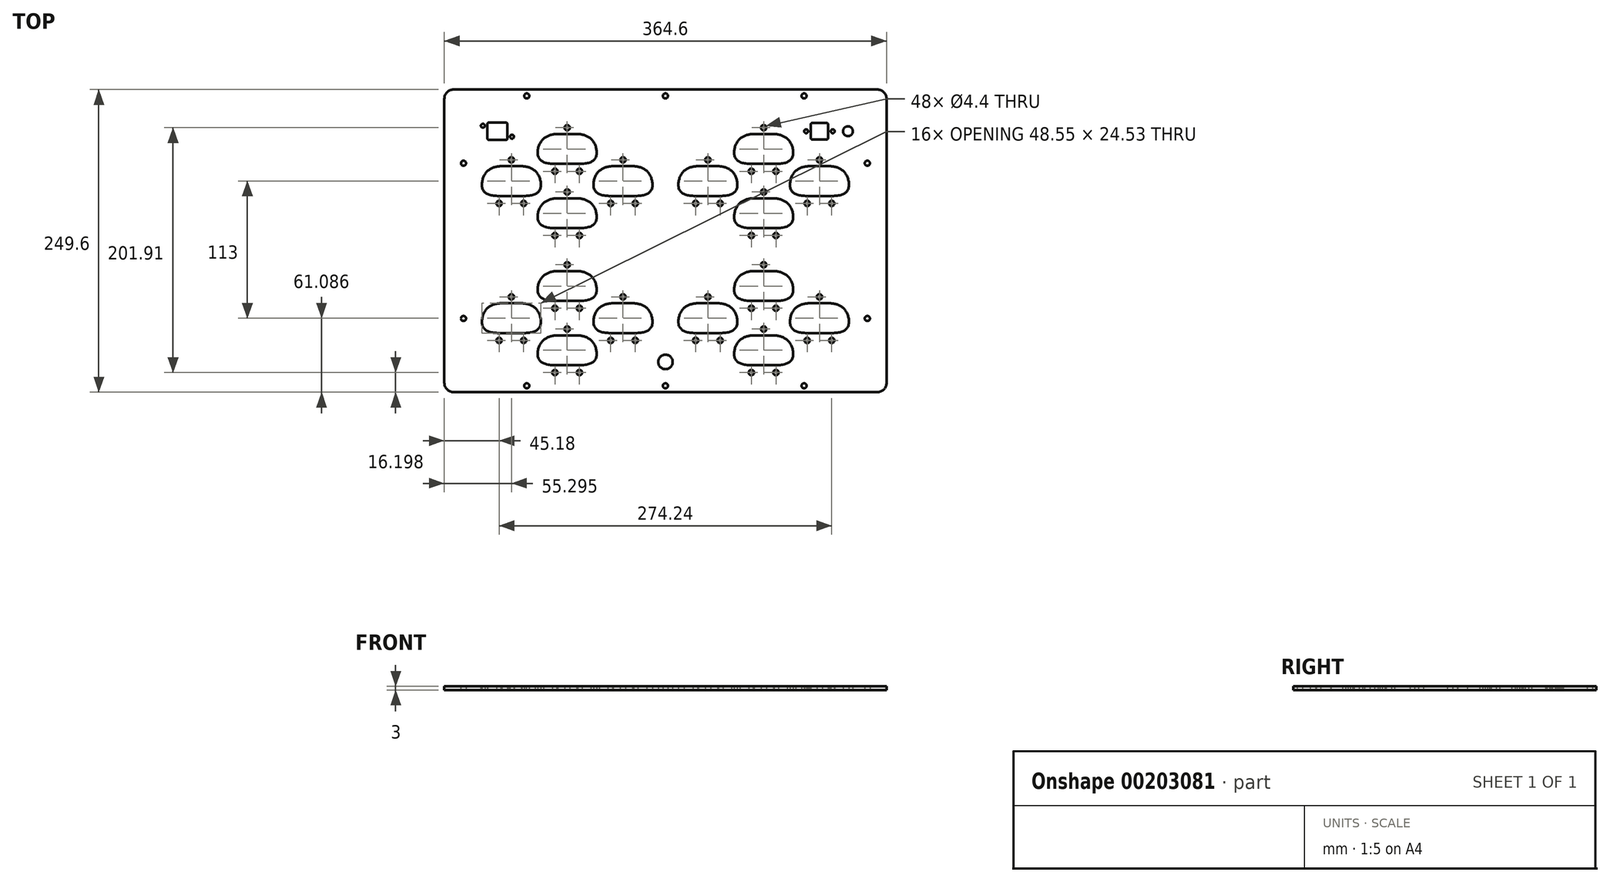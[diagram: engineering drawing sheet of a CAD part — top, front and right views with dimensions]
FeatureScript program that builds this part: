
annotation { "Feature Type Name" : "Feature", "Feature Type Description" : "" }
export const myFeature = defineFeature(function(context is Context, id is Id, definition is map)
    precondition{}
    {
        {
            var Q0;
            Q0=qCreatedBy(makeId("Top.planeOp"),FACE);
            var sketch = newSketch(context, id + "F0", { "sketchPlane" : qUnion([Q0])});
            skLineSegment(sketch, "E0.bottom", {"start": v(-174.5, 124.8) * mm, "end": v(174.5, 124.8) * mm});
            skLineSegment(sketch, "E0.top", {"start": v(-174.5, -124.8) * mm, "end": v(174.5, -124.8) * mm});
            skLineSegment(sketch, "E0.left", {"start": v(-182.3, 117) * mm, "end": v(-182.3, -117) * mm});
            skLineSegment(sketch, "E0.right", {"start": v(182.3, 117) * mm, "end": v(182.3, -117) * mm});
            skPoint(sketch, "E1.visualSharp", {"position": v(-182.3, 124.8) * mm});
            skArc(sketch, "E1.filletArc", {"start": v(-174.5, 124.8) * mm, "mid": v(-180.02, 122.52) * mm, "end": v(-182.3, 117) * mm});
            skPoint(sketch, "E2.visualSharp", {"position": v(182.3, 124.8) * mm});
            skArc(sketch, "E2.filletArc", {"start": v(182.3, 117) * mm, "mid": v(180.02, 122.52) * mm, "end": v(174.5, 124.8) * mm});
            skPoint(sketch, "E3.visualSharp", {"position": v(182.3, -124.8) * mm});
            skArc(sketch, "E3.filletArc", {"start": v(174.5, -124.8) * mm, "mid": v(180.02, -122.52) * mm, "end": v(182.3, -117) * mm});
            skPoint(sketch, "E4.visualSharp", {"position": v(-182.3, -124.8) * mm});
            skArc(sketch, "E4.filletArc", {"start": v(-182.3, -117) * mm, "mid": v(-180.02, -122.52) * mm, "end": v(-174.5, -124.8) * mm});
            skCircle(sketch, "E5", {"center": v(-166.5, -64) * mm, "radius": 2.1 * mm});
            skCircle(sketch, "E6", {"center": v(-166.5, 64) * mm, "radius": 2.1 * mm});
            skCircle(sketch, "E7.MirrorC", {"center": v(166.5, 64) * mm, "radius": 2.1 * mm});
            skCircle(sketch, "E8.MirrorC", {"center": v(166.5, -64) * mm, "radius": 2.1 * mm});
            skCircle(sketch, "E9", {"center": v(-114.33, -119.5) * mm, "radius": 2.1 * mm});
            skCircle(sketch, "E10", {"center": v(0, -119.5) * mm, "radius": 2.1 * mm});
            skCircle(sketch, "E11.MirrorC", {"center": v(114.33, -119.5) * mm, "radius": 2.1 * mm});
            skCircle(sketch, "E12.MirrorC", {"center": v(-114.33, 119.5) * mm, "radius": 2.1 * mm});
            skCircle(sketch, "E13.MirrorC", {"center": v(0, 119.5) * mm, "radius": 2.1 * mm});
            skCircle(sketch, "E14.MirrorC", {"center": v(114.33, 119.5) * mm, "radius": 2.1 * mm});
            skLineSegment(sketch, "E15.1", {"start": v(-135.12, -51.46) * mm, "end": v(-118.9, -51.46) * mm});
            skLineSegment(sketch, "E15.3", {"start": v(-118.9, -51.46) * mm, "end": v(-118.33, -51.45) * mm});
            skArc(sketch, "E15.4", {"start": v(-118.33, -51.45) * mm, "mid": v(-112.6, -52.41) * mm, "end": v(-107.49, -55.2) * mm});
            skArc(sketch, "E15.5", {"start": v(-107.49, -55.2) * mm, "mid": v(-103.73, -60.96) * mm, "end": v(-102.78, -67.78) * mm});
            skLineSegment(sketch, "E15.8", {"start": v(-135.1, -75.97) * mm, "end": v(-118.9, -75.97) * mm});
            skFitSpline(sketch, "E15.9", {"points": [v(-102.78, -67.78) * mm, v(-102.83, -68.48) * mm, v(-103.13, -69.85) * mm, v(-104.12, -71.74) * mm, v(-105.36, -73.07) * mm, v(-106.59, -73.94) * mm, v(-107.95, -74.65) * mm, v(-109.89, -75.3) * mm, v(-112.56, -75.75) * mm, v(-115.56, -75.96) * mm, v(-117.76, -75.98) * mm, v(-118.9, -75.97) * mm]});
            skCircle(sketch, "E16", {"center": v(-127, -46.2) * mm, "radius": 2.2 * mm});
            skCircle(sketch, "E17", {"center": v(-137.12, -82.1) * mm, "radius": 2.2 * mm});
            skCircle(sketch, "E18", {"center": v(-116.88, -82.1) * mm, "radius": 2.2 * mm});
            skFitSpline(sketch, "E19.0", {"points": [v(-151.23, -67.78) * mm, v(-151.18, -68.48) * mm, v(-150.87, -69.85) * mm, v(-149.88, -71.74) * mm, v(-148.63, -73.07) * mm, v(-147.4, -73.93) * mm, v(-146.05, -74.65) * mm, v(-144.11, -75.3) * mm, v(-141.44, -75.75) * mm, v(-138.45, -75.95) * mm, v(-136.25, -75.98) * mm, v(-135.1, -75.97) * mm]});
            skArc(sketch, "E19.1", {"start": v(-146.52, -55.2) * mm, "mid": v(-150.28, -60.96) * mm, "end": v(-151.23, -67.78) * mm});
            skArc(sketch, "E19.2", {"start": v(-135.66, -51.45) * mm, "mid": v(-141.4, -52.41) * mm, "end": v(-146.52, -55.2) * mm});
            skLineSegment(sketch, "E20.0", {"start": v(-135.1, -51.46) * mm, "end": v(-135.66, -51.45) * mm});
            skPoint(sketch, "E21", {"position": v(-156, -112.5) * mm});
            skLineSegment(sketch, "E22.1", {"start": v(-89.12, -77.96) * mm, "end": v(-72.9, -77.96) * mm});
            skLineSegment(sketch, "E22.3", {"start": v(-72.9, -77.96) * mm, "end": v(-72.33, -77.95) * mm});
            skArc(sketch, "E22.4", {"start": v(-72.33, -77.95) * mm, "mid": v(-66.6, -78.91) * mm, "end": v(-61.49, -81.7) * mm});
            skArc(sketch, "E22.5", {"start": v(-61.49, -81.7) * mm, "mid": v(-57.73, -87.46) * mm, "end": v(-56.78, -94.28) * mm});
            skLineSegment(sketch, "E22.8", {"start": v(-89.1, -102.47) * mm, "end": v(-72.9, -102.47) * mm});
            skFitSpline(sketch, "E22.9", {"points": [v(-56.78, -94.28) * mm, v(-56.83, -94.98) * mm, v(-57.13, -96.35) * mm, v(-58.12, -98.24) * mm, v(-59.36, -99.57) * mm, v(-60.58, -100.44) * mm, v(-61.95, -101.15) * mm, v(-63.88, -101.8) * mm, v(-66.56, -102.25) * mm, v(-69.56, -102.45) * mm, v(-71.76, -102.48) * mm, v(-72.9, -102.47) * mm]});
            skCircle(sketch, "E23", {"center": v(-81, -72.7) * mm, "radius": 2.2 * mm});
            skCircle(sketch, "E24", {"center": v(-91.12, -108.6) * mm, "radius": 2.2 * mm});
            skCircle(sketch, "E25", {"center": v(-70.88, -108.6) * mm, "radius": 2.2 * mm});
            skFitSpline(sketch, "E26.0", {"points": [v(-105.23, -94.28) * mm, v(-105.18, -94.98) * mm, v(-104.87, -96.35) * mm, v(-103.88, -98.24) * mm, v(-102.63, -99.57) * mm, v(-101.4, -100.43) * mm, v(-100.05, -101.15) * mm, v(-98.11, -101.8) * mm, v(-95.44, -102.25) * mm, v(-92.45, -102.45) * mm, v(-90.25, -102.48) * mm, v(-89.1, -102.47) * mm]});
            skArc(sketch, "E26.1", {"start": v(-100.52, -81.7) * mm, "mid": v(-104.28, -87.46) * mm, "end": v(-105.23, -94.28) * mm});
            skArc(sketch, "E26.2", {"start": v(-89.66, -77.95) * mm, "mid": v(-95.4, -78.91) * mm, "end": v(-100.52, -81.7) * mm});
            skLineSegment(sketch, "E27.0", {"start": v(-89.1, -77.96) * mm, "end": v(-89.66, -77.95) * mm});
            skLineSegment(sketch, "E28.1", {"start": v(-43.12, -51.46) * mm, "end": v(-26.9, -51.46) * mm});
            skLineSegment(sketch, "E28.3", {"start": v(-26.9, -51.46) * mm, "end": v(-26.33, -51.45) * mm});
            skArc(sketch, "E28.4", {"start": v(-26.33, -51.45) * mm, "mid": v(-20.6, -52.41) * mm, "end": v(-15.49, -55.2) * mm});
            skArc(sketch, "E28.5", {"start": v(-15.49, -55.2) * mm, "mid": v(-11.73, -60.96) * mm, "end": v(-10.78, -67.78) * mm});
            skLineSegment(sketch, "E28.8", {"start": v(-43.1, -75.97) * mm, "end": v(-26.9, -75.97) * mm});
            skFitSpline(sketch, "E28.9", {"points": [v(-10.78, -67.78) * mm, v(-10.83, -68.48) * mm, v(-11.13, -69.85) * mm, v(-12.12, -71.74) * mm, v(-13.36, -73.07) * mm, v(-14.59, -73.94) * mm, v(-15.95, -74.65) * mm, v(-17.89, -75.3) * mm, v(-20.56, -75.75) * mm, v(-23.56, -75.96) * mm, v(-25.76, -75.98) * mm, v(-26.9, -75.97) * mm]});
            skCircle(sketch, "E29", {"center": v(-35, -46.2) * mm, "radius": 2.2 * mm});
            skCircle(sketch, "E30", {"center": v(-45.12, -82.1) * mm, "radius": 2.2 * mm});
            skCircle(sketch, "E31", {"center": v(-24.88, -82.1) * mm, "radius": 2.2 * mm});
            skFitSpline(sketch, "E32.0", {"points": [v(-59.23, -67.78) * mm, v(-59.18, -68.48) * mm, v(-58.87, -69.85) * mm, v(-57.88, -71.74) * mm, v(-56.63, -73.07) * mm, v(-55.4, -73.93) * mm, v(-54.05, -74.65) * mm, v(-52.11, -75.3) * mm, v(-49.44, -75.75) * mm, v(-46.45, -75.95) * mm, v(-44.25, -75.98) * mm, v(-43.1, -75.97) * mm]});
            skArc(sketch, "E32.1", {"start": v(-54.52, -55.2) * mm, "mid": v(-58.28, -60.96) * mm, "end": v(-59.23, -67.78) * mm});
            skArc(sketch, "E32.2", {"start": v(-43.66, -51.45) * mm, "mid": v(-49.4, -52.41) * mm, "end": v(-54.52, -55.2) * mm});
            skLineSegment(sketch, "E33.0", {"start": v(-43.1, -51.46) * mm, "end": v(-43.66, -51.45) * mm});
            skLineSegment(sketch, "E34.1", {"start": v(-89.12, -24.96) * mm, "end": v(-72.9, -24.96) * mm});
            skLineSegment(sketch, "E34.3", {"start": v(-72.9, -24.96) * mm, "end": v(-72.33, -24.95) * mm});
            skArc(sketch, "E34.4", {"start": v(-72.33, -24.95) * mm, "mid": v(-66.6, -25.91) * mm, "end": v(-61.49, -28.7) * mm});
            skArc(sketch, "E34.5", {"start": v(-61.49, -28.7) * mm, "mid": v(-57.73, -34.46) * mm, "end": v(-56.78, -41.28) * mm});
            skLineSegment(sketch, "E34.8", {"start": v(-89.1, -49.47) * mm, "end": v(-72.9, -49.47) * mm});
            skFitSpline(sketch, "E34.9", {"points": [v(-56.78, -41.28) * mm, v(-56.83, -41.98) * mm, v(-57.13, -43.35) * mm, v(-58.12, -45.24) * mm, v(-59.36, -46.57) * mm, v(-60.59, -47.44) * mm, v(-61.95, -48.15) * mm, v(-63.89, -48.8) * mm, v(-66.56, -49.25) * mm, v(-69.56, -49.46) * mm, v(-71.76, -49.48) * mm, v(-72.9, -49.47) * mm]});
            skCircle(sketch, "E35", {"center": v(-81, -19.7) * mm, "radius": 2.2 * mm});
            skCircle(sketch, "E36", {"center": v(-91.12, -55.6) * mm, "radius": 2.2 * mm});
            skCircle(sketch, "E37", {"center": v(-70.88, -55.6) * mm, "radius": 2.2 * mm});
            skFitSpline(sketch, "E38.0", {"points": [v(-105.23, -41.28) * mm, v(-105.18, -41.98) * mm, v(-104.87, -43.35) * mm, v(-103.88, -45.24) * mm, v(-102.63, -46.57) * mm, v(-101.4, -47.43) * mm, v(-100.05, -48.15) * mm, v(-98.11, -48.8) * mm, v(-95.44, -49.25) * mm, v(-92.45, -49.45) * mm, v(-90.25, -49.48) * mm, v(-89.1, -49.47) * mm]});
            skArc(sketch, "E38.1", {"start": v(-100.52, -28.7) * mm, "mid": v(-104.28, -34.46) * mm, "end": v(-105.23, -41.28) * mm});
            skArc(sketch, "E38.2", {"start": v(-89.66, -24.95) * mm, "mid": v(-95.4, -25.91) * mm, "end": v(-100.52, -28.7) * mm});
            skLineSegment(sketch, "E39.0", {"start": v(-89.1, -24.96) * mm, "end": v(-89.66, -24.95) * mm});
            skLineSegment(sketch, "E40.1", {"start": v(-135.12, 61.54) * mm, "end": v(-118.9, 61.54) * mm});
            skLineSegment(sketch, "E40.3", {"start": v(-118.9, 61.54) * mm, "end": v(-118.33, 61.55) * mm});
            skArc(sketch, "E40.4", {"start": v(-118.33, 61.55) * mm, "mid": v(-112.6, 60.59) * mm, "end": v(-107.49, 57.8) * mm});
            skArc(sketch, "E40.5", {"start": v(-107.49, 57.8) * mm, "mid": v(-103.73, 52.04) * mm, "end": v(-102.78, 45.22) * mm});
            skLineSegment(sketch, "E40.8", {"start": v(-135.1, 37.03) * mm, "end": v(-118.9, 37.03) * mm});
            skFitSpline(sketch, "E40.9", {"points": [v(-102.78, 45.22) * mm, v(-102.83, 44.52) * mm, v(-103.13, 43.15) * mm, v(-104.12, 41.26) * mm, v(-105.36, 39.93) * mm, v(-106.59, 39.06) * mm, v(-107.95, 38.35) * mm, v(-109.89, 37.7) * mm, v(-112.56, 37.25) * mm, v(-115.56, 37.04) * mm, v(-117.76, 37.02) * mm, v(-118.9, 37.03) * mm]});
            skCircle(sketch, "E41", {"center": v(-127, 66.8) * mm, "radius": 2.2 * mm});
            skCircle(sketch, "E42", {"center": v(-137.12, 30.9) * mm, "radius": 2.2 * mm});
            skCircle(sketch, "E43", {"center": v(-116.88, 30.9) * mm, "radius": 2.2 * mm});
            skFitSpline(sketch, "E44.0", {"points": [v(-151.23, 45.22) * mm, v(-151.18, 44.52) * mm, v(-150.87, 43.15) * mm, v(-149.88, 41.26) * mm, v(-148.63, 39.93) * mm, v(-147.4, 39.07) * mm, v(-146.05, 38.35) * mm, v(-144.11, 37.7) * mm, v(-141.44, 37.25) * mm, v(-138.45, 37.05) * mm, v(-136.25, 37.02) * mm, v(-135.1, 37.03) * mm]});
            skArc(sketch, "E44.1", {"start": v(-146.52, 57.8) * mm, "mid": v(-150.28, 52.04) * mm, "end": v(-151.23, 45.22) * mm});
            skArc(sketch, "E44.2", {"start": v(-135.66, 61.55) * mm, "mid": v(-141.4, 60.59) * mm, "end": v(-146.52, 57.8) * mm});
            skLineSegment(sketch, "E45.0", {"start": v(-135.1, 61.54) * mm, "end": v(-135.66, 61.55) * mm});
            skLineSegment(sketch, "E46.1", {"start": v(-89.12, 35.04) * mm, "end": v(-72.9, 35.04) * mm});
            skLineSegment(sketch, "E46.3", {"start": v(-72.9, 35.04) * mm, "end": v(-72.33, 35.05) * mm});
            skArc(sketch, "E46.4", {"start": v(-72.33, 35.05) * mm, "mid": v(-66.6, 34.09) * mm, "end": v(-61.49, 31.3) * mm});
            skArc(sketch, "E46.5", {"start": v(-61.49, 31.3) * mm, "mid": v(-57.73, 25.54) * mm, "end": v(-56.78, 18.72) * mm});
            skLineSegment(sketch, "E46.8", {"start": v(-89.1, 10.53) * mm, "end": v(-72.9, 10.53) * mm});
            skFitSpline(sketch, "E46.9", {"points": [v(-56.78, 18.72) * mm, v(-56.83, 18.02) * mm, v(-57.13, 16.65) * mm, v(-58.12, 14.76) * mm, v(-59.36, 13.43) * mm, v(-60.59, 12.56) * mm, v(-61.95, 11.85) * mm, v(-63.89, 11.2) * mm, v(-66.56, 10.75) * mm, v(-69.56, 10.54) * mm, v(-71.76, 10.52) * mm, v(-72.9, 10.53) * mm]});
            skCircle(sketch, "E47", {"center": v(-81, 40.3) * mm, "radius": 2.2 * mm});
            skCircle(sketch, "E48", {"center": v(-91.12, 4.4) * mm, "radius": 2.2 * mm});
            skCircle(sketch, "E49", {"center": v(-70.88, 4.4) * mm, "radius": 2.2 * mm});
            skFitSpline(sketch, "E50.0", {"points": [v(-105.23, 18.72) * mm, v(-105.18, 18.02) * mm, v(-104.87, 16.65) * mm, v(-103.88, 14.76) * mm, v(-102.63, 13.43) * mm, v(-101.4, 12.57) * mm, v(-100.05, 11.85) * mm, v(-98.11, 11.2) * mm, v(-95.44, 10.75) * mm, v(-92.45, 10.55) * mm, v(-90.25, 10.52) * mm, v(-89.1, 10.53) * mm]});
            skArc(sketch, "E50.1", {"start": v(-100.52, 31.3) * mm, "mid": v(-104.28, 25.54) * mm, "end": v(-105.23, 18.72) * mm});
            skArc(sketch, "E50.2", {"start": v(-89.66, 35.05) * mm, "mid": v(-95.4, 34.09) * mm, "end": v(-100.52, 31.3) * mm});
            skLineSegment(sketch, "E51.0", {"start": v(-89.1, 35.04) * mm, "end": v(-89.66, 35.05) * mm});
            skLineSegment(sketch, "E52.1", {"start": v(-43.12, 61.54) * mm, "end": v(-26.9, 61.54) * mm});
            skLineSegment(sketch, "E52.3", {"start": v(-26.9, 61.54) * mm, "end": v(-26.33, 61.55) * mm});
            skArc(sketch, "E52.4", {"start": v(-26.33, 61.55) * mm, "mid": v(-20.6, 60.59) * mm, "end": v(-15.49, 57.8) * mm});
            skArc(sketch, "E52.5", {"start": v(-15.49, 57.8) * mm, "mid": v(-11.73, 52.04) * mm, "end": v(-10.77, 45.22) * mm});
            skLineSegment(sketch, "E52.8", {"start": v(-43.1, 37.03) * mm, "end": v(-26.9, 37.03) * mm});
            skFitSpline(sketch, "E52.9", {"points": [v(-10.77, 45.22) * mm, v(-10.83, 44.52) * mm, v(-11.13, 43.15) * mm, v(-12.12, 41.26) * mm, v(-13.36, 39.93) * mm, v(-14.58, 39.06) * mm, v(-15.95, 38.35) * mm, v(-17.88, 37.7) * mm, v(-20.56, 37.25) * mm, v(-23.56, 37.04) * mm, v(-25.76, 37.02) * mm, v(-26.9, 37.03) * mm]});
            skCircle(sketch, "E53", {"center": v(-35, 66.8) * mm, "radius": 2.2 * mm});
            skCircle(sketch, "E54", {"center": v(-45.12, 30.9) * mm, "radius": 2.2 * mm});
            skCircle(sketch, "E55", {"center": v(-24.88, 30.9) * mm, "radius": 2.2 * mm});
            skFitSpline(sketch, "E56.0", {"points": [v(-59.23, 45.22) * mm, v(-59.18, 44.52) * mm, v(-58.87, 43.15) * mm, v(-57.88, 41.27) * mm, v(-56.63, 39.93) * mm, v(-55.4, 39.07) * mm, v(-54.05, 38.35) * mm, v(-52.11, 37.7) * mm, v(-49.44, 37.26) * mm, v(-46.45, 37.05) * mm, v(-44.25, 37.02) * mm, v(-43.1, 37.03) * mm]});
            skArc(sketch, "E56.1", {"start": v(-54.52, 57.8) * mm, "mid": v(-58.28, 52.03) * mm, "end": v(-59.23, 45.22) * mm});
            skArc(sketch, "E56.2", {"start": v(-43.66, 61.55) * mm, "mid": v(-49.4, 60.59) * mm, "end": v(-54.52, 57.8) * mm});
            skLineSegment(sketch, "E57.0", {"start": v(-43.1, 61.54) * mm, "end": v(-43.66, 61.55) * mm});
            skLineSegment(sketch, "E58.1", {"start": v(-89.12, 88.04) * mm, "end": v(-72.9, 88.04) * mm});
            skLineSegment(sketch, "E58.3", {"start": v(-72.9, 88.04) * mm, "end": v(-72.33, 88.05) * mm});
            skArc(sketch, "E58.4", {"start": v(-72.33, 88.05) * mm, "mid": v(-66.6, 87.09) * mm, "end": v(-61.49, 84.3) * mm});
            skArc(sketch, "E58.5", {"start": v(-61.49, 84.3) * mm, "mid": v(-57.73, 78.54) * mm, "end": v(-56.78, 71.72) * mm});
            skLineSegment(sketch, "E58.8", {"start": v(-89.1, 63.53) * mm, "end": v(-72.9, 63.53) * mm});
            skFitSpline(sketch, "E58.9", {"points": [v(-56.78, 71.72) * mm, v(-56.83, 71.02) * mm, v(-57.13, 69.65) * mm, v(-58.12, 67.76) * mm, v(-59.36, 66.43) * mm, v(-60.59, 65.56) * mm, v(-61.95, 64.85) * mm, v(-63.89, 64.2) * mm, v(-66.56, 63.75) * mm, v(-69.56, 63.54) * mm, v(-71.76, 63.52) * mm, v(-72.9, 63.53) * mm]});
            skCircle(sketch, "E59", {"center": v(-81, 93.3) * mm, "radius": 2.2 * mm});
            skCircle(sketch, "E60", {"center": v(-91.12, 57.4) * mm, "radius": 2.2 * mm});
            skCircle(sketch, "E61", {"center": v(-70.88, 57.4) * mm, "radius": 2.2 * mm});
            skFitSpline(sketch, "E62.0", {"points": [v(-105.23, 71.72) * mm, v(-105.18, 71.02) * mm, v(-104.87, 69.65) * mm, v(-103.88, 67.76) * mm, v(-102.63, 66.43) * mm, v(-101.4, 65.57) * mm, v(-100.05, 64.85) * mm, v(-98.11, 64.2) * mm, v(-95.44, 63.75) * mm, v(-92.45, 63.55) * mm, v(-90.25, 63.52) * mm, v(-89.1, 63.53) * mm]});
            skArc(sketch, "E62.1", {"start": v(-100.52, 84.3) * mm, "mid": v(-104.28, 78.54) * mm, "end": v(-105.23, 71.72) * mm});
            skArc(sketch, "E62.2", {"start": v(-89.66, 88.05) * mm, "mid": v(-95.4, 87.09) * mm, "end": v(-100.52, 84.3) * mm});
            skLineSegment(sketch, "E63.0", {"start": v(-89.1, 88.04) * mm, "end": v(-89.66, 88.05) * mm});
            skLineSegment(sketch, "E64.1", {"start": v(26.88, 61.54) * mm, "end": v(43.1, 61.54) * mm});
            skLineSegment(sketch, "E64.3", {"start": v(43.1, 61.54) * mm, "end": v(43.67, 61.55) * mm});
            skArc(sketch, "E64.4", {"start": v(43.67, 61.55) * mm, "mid": v(49.4, 60.59) * mm, "end": v(54.51, 57.8) * mm});
            skArc(sketch, "E64.5", {"start": v(54.51, 57.8) * mm, "mid": v(58.27, 52.04) * mm, "end": v(59.22, 45.22) * mm});
            skLineSegment(sketch, "E64.8", {"start": v(26.9, 37.03) * mm, "end": v(43.1, 37.03) * mm});
            skFitSpline(sketch, "E64.9", {"points": [v(59.22, 45.22) * mm, v(59.17, 44.52) * mm, v(58.87, 43.15) * mm, v(57.88, 41.26) * mm, v(56.64, 39.93) * mm, v(55.42, 39.06) * mm, v(54.05, 38.35) * mm, v(52.12, 37.7) * mm, v(49.44, 37.25) * mm, v(46.44, 37.05) * mm, v(44.24, 37.02) * mm, v(43.1, 37.03) * mm]});
            skCircle(sketch, "E65", {"center": v(35, 66.8) * mm, "radius": 2.2 * mm});
            skCircle(sketch, "E66", {"center": v(24.88, 30.9) * mm, "radius": 2.2 * mm});
            skCircle(sketch, "E67", {"center": v(45.12, 30.9) * mm, "radius": 2.2 * mm});
            skFitSpline(sketch, "E68.0", {"points": [v(10.77, 45.22) * mm, v(10.82, 44.52) * mm, v(11.13, 43.15) * mm, v(12.12, 41.26) * mm, v(13.37, 39.93) * mm, v(14.6, 39.07) * mm, v(15.95, 38.35) * mm, v(17.89, 37.7) * mm, v(20.56, 37.25) * mm, v(23.55, 37.05) * mm, v(25.75, 37.02) * mm, v(26.9, 37.03) * mm]});
            skArc(sketch, "E68.1", {"start": v(15.48, 57.8) * mm, "mid": v(11.72, 52.04) * mm, "end": v(10.77, 45.22) * mm});
            skArc(sketch, "E68.2", {"start": v(26.34, 61.55) * mm, "mid": v(20.6, 60.59) * mm, "end": v(15.48, 57.8) * mm});
            skLineSegment(sketch, "E69.0", {"start": v(26.9, 61.54) * mm, "end": v(26.34, 61.55) * mm});
            skLineSegment(sketch, "E70.1", {"start": v(72.88, 35.04) * mm, "end": v(89.1, 35.04) * mm});
            skLineSegment(sketch, "E70.3", {"start": v(89.1, 35.04) * mm, "end": v(89.67, 35.05) * mm});
            skArc(sketch, "E70.4", {"start": v(89.67, 35.05) * mm, "mid": v(95.4, 34.09) * mm, "end": v(100.51, 31.3) * mm});
            skArc(sketch, "E70.5", {"start": v(100.51, 31.3) * mm, "mid": v(104.27, 25.54) * mm, "end": v(105.22, 18.72) * mm});
            skLineSegment(sketch, "E70.8", {"start": v(72.9, 10.53) * mm, "end": v(89.1, 10.53) * mm});
            skFitSpline(sketch, "E70.9", {"points": [v(105.22, 18.72) * mm, v(105.17, 18.02) * mm, v(104.87, 16.65) * mm, v(103.88, 14.76) * mm, v(102.64, 13.43) * mm, v(101.42, 12.56) * mm, v(100.05, 11.85) * mm, v(98.12, 11.2) * mm, v(95.44, 10.75) * mm, v(92.44, 10.55) * mm, v(90.24, 10.52) * mm, v(89.1, 10.53) * mm]});
            skCircle(sketch, "E71", {"center": v(81, 40.3) * mm, "radius": 2.2 * mm});
            skCircle(sketch, "E72", {"center": v(70.88, 4.4) * mm, "radius": 2.2 * mm});
            skCircle(sketch, "E73", {"center": v(91.12, 4.4) * mm, "radius": 2.2 * mm});
            skFitSpline(sketch, "E74.0", {"points": [v(56.77, 18.72) * mm, v(56.82, 18.02) * mm, v(57.13, 16.65) * mm, v(58.12, 14.76) * mm, v(59.37, 13.43) * mm, v(60.6, 12.57) * mm, v(61.95, 11.85) * mm, v(63.89, 11.2) * mm, v(66.56, 10.75) * mm, v(69.55, 10.55) * mm, v(71.75, 10.52) * mm, v(72.9, 10.53) * mm]});
            skArc(sketch, "E74.1", {"start": v(61.48, 31.3) * mm, "mid": v(57.72, 25.54) * mm, "end": v(56.77, 18.72) * mm});
            skArc(sketch, "E74.2", {"start": v(72.34, 35.05) * mm, "mid": v(66.6, 34.09) * mm, "end": v(61.48, 31.3) * mm});
            skLineSegment(sketch, "E75.0", {"start": v(72.9, 35.04) * mm, "end": v(72.34, 35.05) * mm});
            skLineSegment(sketch, "E76.1", {"start": v(118.88, 61.54) * mm, "end": v(135.1, 61.54) * mm});
            skLineSegment(sketch, "E76.3", {"start": v(135.1, 61.54) * mm, "end": v(135.67, 61.55) * mm});
            skArc(sketch, "E76.4", {"start": v(135.67, 61.55) * mm, "mid": v(141.4, 60.59) * mm, "end": v(146.51, 57.8) * mm});
            skArc(sketch, "E76.5", {"start": v(146.51, 57.8) * mm, "mid": v(150.27, 52.04) * mm, "end": v(151.22, 45.22) * mm});
            skLineSegment(sketch, "E76.8", {"start": v(118.9, 37.03) * mm, "end": v(135.1, 37.03) * mm});
            skFitSpline(sketch, "E76.9", {"points": [v(151.22, 45.22) * mm, v(151.17, 44.52) * mm, v(150.87, 43.15) * mm, v(149.88, 41.26) * mm, v(148.64, 39.93) * mm, v(147.42, 39.06) * mm, v(146.05, 38.35) * mm, v(144.12, 37.7) * mm, v(141.44, 37.25) * mm, v(138.44, 37.05) * mm, v(136.24, 37.02) * mm, v(135.1, 37.03) * mm]});
            skCircle(sketch, "E77", {"center": v(127, 66.8) * mm, "radius": 2.2 * mm});
            skCircle(sketch, "E78", {"center": v(116.88, 30.9) * mm, "radius": 2.2 * mm});
            skCircle(sketch, "E79", {"center": v(137.12, 30.9) * mm, "radius": 2.2 * mm});
            skFitSpline(sketch, "E80.0", {"points": [v(102.77, 45.22) * mm, v(102.82, 44.52) * mm, v(103.13, 43.15) * mm, v(104.12, 41.26) * mm, v(105.37, 39.93) * mm, v(106.6, 39.07) * mm, v(107.95, 38.35) * mm, v(109.89, 37.7) * mm, v(112.56, 37.25) * mm, v(115.55, 37.05) * mm, v(117.75, 37.02) * mm, v(118.9, 37.03) * mm]});
            skArc(sketch, "E80.1", {"start": v(107.48, 57.8) * mm, "mid": v(103.72, 52.04) * mm, "end": v(102.77, 45.22) * mm});
            skArc(sketch, "E80.2", {"start": v(118.34, 61.55) * mm, "mid": v(112.6, 60.59) * mm, "end": v(107.48, 57.8) * mm});
            skLineSegment(sketch, "E81.0", {"start": v(118.9, 61.54) * mm, "end": v(118.34, 61.55) * mm});
            skLineSegment(sketch, "E82.1", {"start": v(72.88, 88.04) * mm, "end": v(89.1, 88.04) * mm});
            skLineSegment(sketch, "E82.3", {"start": v(89.1, 88.04) * mm, "end": v(89.67, 88.05) * mm});
            skArc(sketch, "E82.4", {"start": v(89.67, 88.05) * mm, "mid": v(95.4, 87.09) * mm, "end": v(100.51, 84.3) * mm});
            skArc(sketch, "E82.5", {"start": v(100.51, 84.3) * mm, "mid": v(104.27, 78.54) * mm, "end": v(105.22, 71.72) * mm});
            skLineSegment(sketch, "E82.8", {"start": v(72.9, 63.53) * mm, "end": v(89.1, 63.53) * mm});
            skFitSpline(sketch, "E82.9", {"points": [v(105.22, 71.72) * mm, v(105.17, 71.02) * mm, v(104.87, 69.65) * mm, v(103.88, 67.76) * mm, v(102.64, 66.43) * mm, v(101.42, 65.56) * mm, v(100.05, 64.85) * mm, v(98.12, 64.2) * mm, v(95.44, 63.75) * mm, v(92.44, 63.55) * mm, v(90.24, 63.52) * mm, v(89.1, 63.53) * mm]});
            skCircle(sketch, "E83", {"center": v(81, 93.3) * mm, "radius": 2.2 * mm});
            skCircle(sketch, "E84", {"center": v(70.88, 57.4) * mm, "radius": 2.2 * mm});
            skCircle(sketch, "E85", {"center": v(91.12, 57.4) * mm, "radius": 2.2 * mm});
            skFitSpline(sketch, "E86.0", {"points": [v(56.77, 71.72) * mm, v(56.82, 71.02) * mm, v(57.13, 69.65) * mm, v(58.12, 67.76) * mm, v(59.37, 66.43) * mm, v(60.6, 65.57) * mm, v(61.95, 64.85) * mm, v(63.89, 64.2) * mm, v(66.56, 63.75) * mm, v(69.55, 63.55) * mm, v(71.75, 63.52) * mm, v(72.9, 63.53) * mm]});
            skArc(sketch, "E86.1", {"start": v(61.48, 84.3) * mm, "mid": v(57.72, 78.54) * mm, "end": v(56.77, 71.72) * mm});
            skArc(sketch, "E86.2", {"start": v(72.34, 88.05) * mm, "mid": v(66.6, 87.09) * mm, "end": v(61.48, 84.3) * mm});
            skLineSegment(sketch, "E87.0", {"start": v(72.9, 88.04) * mm, "end": v(72.34, 88.05) * mm});
            skLineSegment(sketch, "E88.1", {"start": v(26.88, -51.46) * mm, "end": v(43.1, -51.46) * mm});
            skLineSegment(sketch, "E88.3", {"start": v(43.1, -51.46) * mm, "end": v(43.67, -51.45) * mm});
            skArc(sketch, "E88.4", {"start": v(43.67, -51.45) * mm, "mid": v(49.4, -52.41) * mm, "end": v(54.51, -55.2) * mm});
            skArc(sketch, "E88.5", {"start": v(54.51, -55.2) * mm, "mid": v(58.27, -60.96) * mm, "end": v(59.22, -67.78) * mm});
            skLineSegment(sketch, "E88.8", {"start": v(26.9, -75.97) * mm, "end": v(43.1, -75.97) * mm});
            skFitSpline(sketch, "E88.9", {"points": [v(59.22, -67.78) * mm, v(59.17, -68.48) * mm, v(58.87, -69.85) * mm, v(57.88, -71.74) * mm, v(56.64, -73.07) * mm, v(55.41, -73.94) * mm, v(54.05, -74.65) * mm, v(52.11, -75.3) * mm, v(49.44, -75.75) * mm, v(46.44, -75.96) * mm, v(44.24, -75.98) * mm, v(43.1, -75.97) * mm]});
            skCircle(sketch, "E89", {"center": v(35, -46.2) * mm, "radius": 2.2 * mm});
            skCircle(sketch, "E90", {"center": v(24.88, -82.1) * mm, "radius": 2.2 * mm});
            skCircle(sketch, "E91", {"center": v(45.12, -82.1) * mm, "radius": 2.2 * mm});
            skFitSpline(sketch, "E92.0", {"points": [v(10.77, -67.78) * mm, v(10.82, -68.48) * mm, v(11.13, -69.85) * mm, v(12.12, -71.74) * mm, v(13.37, -73.07) * mm, v(14.6, -73.93) * mm, v(15.95, -74.65) * mm, v(17.89, -75.3) * mm, v(20.56, -75.75) * mm, v(23.55, -75.95) * mm, v(25.75, -75.98) * mm, v(26.9, -75.97) * mm]});
            skArc(sketch, "E92.1", {"start": v(15.48, -55.2) * mm, "mid": v(11.72, -60.96) * mm, "end": v(10.77, -67.78) * mm});
            skArc(sketch, "E92.2", {"start": v(26.34, -51.45) * mm, "mid": v(20.6, -52.41) * mm, "end": v(15.48, -55.2) * mm});
            skLineSegment(sketch, "E93.0", {"start": v(26.9, -51.46) * mm, "end": v(26.34, -51.45) * mm});
            skLineSegment(sketch, "E94.1", {"start": v(72.88, -77.96) * mm, "end": v(89.1, -77.96) * mm});
            skLineSegment(sketch, "E94.3", {"start": v(89.1, -77.96) * mm, "end": v(89.67, -77.95) * mm});
            skArc(sketch, "E94.4", {"start": v(89.67, -77.95) * mm, "mid": v(95.4, -78.91) * mm, "end": v(100.51, -81.7) * mm});
            skArc(sketch, "E94.5", {"start": v(100.51, -81.7) * mm, "mid": v(104.27, -87.46) * mm, "end": v(105.22, -94.28) * mm});
            skLineSegment(sketch, "E94.8", {"start": v(72.9, -102.47) * mm, "end": v(89.1, -102.47) * mm});
            skFitSpline(sketch, "E94.9", {"points": [v(105.22, -94.28) * mm, v(105.17, -94.98) * mm, v(104.87, -96.35) * mm, v(103.88, -98.24) * mm, v(102.64, -99.57) * mm, v(101.41, -100.44) * mm, v(100.05, -101.15) * mm, v(98.11, -101.8) * mm, v(95.44, -102.25) * mm, v(92.44, -102.46) * mm, v(90.24, -102.48) * mm, v(89.1, -102.47) * mm]});
            skCircle(sketch, "E95", {"center": v(81, -72.7) * mm, "radius": 2.2 * mm});
            skCircle(sketch, "E96", {"center": v(70.88, -108.6) * mm, "radius": 2.2 * mm});
            skCircle(sketch, "E97", {"center": v(91.12, -108.6) * mm, "radius": 2.2 * mm});
            skFitSpline(sketch, "E98.0", {"points": [v(56.77, -94.28) * mm, v(56.82, -94.98) * mm, v(57.13, -96.35) * mm, v(58.12, -98.24) * mm, v(59.37, -99.57) * mm, v(60.6, -100.43) * mm, v(61.95, -101.15) * mm, v(63.89, -101.8) * mm, v(66.56, -102.25) * mm, v(69.55, -102.45) * mm, v(71.75, -102.48) * mm, v(72.9, -102.47) * mm]});
            skArc(sketch, "E98.1", {"start": v(61.48, -81.7) * mm, "mid": v(57.72, -87.46) * mm, "end": v(56.77, -94.28) * mm});
            skArc(sketch, "E98.2", {"start": v(72.34, -77.95) * mm, "mid": v(66.6, -78.91) * mm, "end": v(61.48, -81.7) * mm});
            skLineSegment(sketch, "E99.0", {"start": v(72.9, -77.96) * mm, "end": v(72.34, -77.95) * mm});
            skLineSegment(sketch, "E100.1", {"start": v(118.88, -51.46) * mm, "end": v(135.1, -51.46) * mm});
            skLineSegment(sketch, "E100.3", {"start": v(135.1, -51.46) * mm, "end": v(135.67, -51.45) * mm});
            skArc(sketch, "E100.4", {"start": v(135.67, -51.45) * mm, "mid": v(141.4, -52.41) * mm, "end": v(146.51, -55.2) * mm});
            skArc(sketch, "E100.5", {"start": v(146.51, -55.2) * mm, "mid": v(150.27, -60.96) * mm, "end": v(151.22, -67.78) * mm});
            skLineSegment(sketch, "E100.8", {"start": v(118.9, -75.97) * mm, "end": v(135.1, -75.97) * mm});
            skFitSpline(sketch, "E100.9", {"points": [v(151.22, -67.78) * mm, v(151.17, -68.48) * mm, v(150.87, -69.85) * mm, v(149.88, -71.74) * mm, v(148.64, -73.07) * mm, v(147.41, -73.94) * mm, v(146.05, -74.65) * mm, v(144.11, -75.3) * mm, v(141.44, -75.75) * mm, v(138.44, -75.96) * mm, v(136.24, -75.98) * mm, v(135.1, -75.97) * mm]});
            skCircle(sketch, "E101", {"center": v(127, -46.2) * mm, "radius": 2.2 * mm});
            skCircle(sketch, "E102", {"center": v(116.88, -82.1) * mm, "radius": 2.2 * mm});
            skCircle(sketch, "E103", {"center": v(137.12, -82.1) * mm, "radius": 2.2 * mm});
            skFitSpline(sketch, "E104.0", {"points": [v(102.77, -67.78) * mm, v(102.82, -68.48) * mm, v(103.13, -69.85) * mm, v(104.12, -71.74) * mm, v(105.37, -73.07) * mm, v(106.6, -73.93) * mm, v(107.95, -74.65) * mm, v(109.89, -75.3) * mm, v(112.56, -75.75) * mm, v(115.55, -75.95) * mm, v(117.75, -75.98) * mm, v(118.9, -75.97) * mm]});
            skArc(sketch, "E104.1", {"start": v(107.48, -55.2) * mm, "mid": v(103.72, -60.96) * mm, "end": v(102.77, -67.78) * mm});
            skArc(sketch, "E104.2", {"start": v(118.34, -51.45) * mm, "mid": v(112.6, -52.41) * mm, "end": v(107.48, -55.2) * mm});
            skLineSegment(sketch, "E105.0", {"start": v(118.9, -51.46) * mm, "end": v(118.34, -51.45) * mm});
            skLineSegment(sketch, "E106.1", {"start": v(72.88, -24.96) * mm, "end": v(89.1, -24.96) * mm});
            skLineSegment(sketch, "E106.3", {"start": v(89.1, -24.96) * mm, "end": v(89.67, -24.95) * mm});
            skArc(sketch, "E106.4", {"start": v(89.67, -24.95) * mm, "mid": v(95.4, -25.91) * mm, "end": v(100.51, -28.7) * mm});
            skArc(sketch, "E106.5", {"start": v(100.51, -28.7) * mm, "mid": v(104.27, -34.46) * mm, "end": v(105.22, -41.28) * mm});
            skLineSegment(sketch, "E106.8", {"start": v(72.9, -49.47) * mm, "end": v(89.1, -49.47) * mm});
            skFitSpline(sketch, "E106.9", {"points": [v(105.22, -41.28) * mm, v(105.17, -41.98) * mm, v(104.87, -43.35) * mm, v(103.88, -45.24) * mm, v(102.64, -46.57) * mm, v(101.41, -47.44) * mm, v(100.05, -48.15) * mm, v(98.11, -48.8) * mm, v(95.44, -49.25) * mm, v(92.44, -49.46) * mm, v(90.24, -49.48) * mm, v(89.1, -49.47) * mm]});
            skCircle(sketch, "E107", {"center": v(81, -19.7) * mm, "radius": 2.2 * mm});
            skCircle(sketch, "E108", {"center": v(70.88, -55.6) * mm, "radius": 2.2 * mm});
            skCircle(sketch, "E109", {"center": v(91.12, -55.6) * mm, "radius": 2.2 * mm});
            skFitSpline(sketch, "E110.0", {"points": [v(56.77, -41.28) * mm, v(56.82, -41.98) * mm, v(57.13, -43.35) * mm, v(58.12, -45.24) * mm, v(59.37, -46.57) * mm, v(60.6, -47.43) * mm, v(61.95, -48.15) * mm, v(63.89, -48.8) * mm, v(66.56, -49.25) * mm, v(69.55, -49.45) * mm, v(71.75, -49.48) * mm, v(72.9, -49.47) * mm]});
            skArc(sketch, "E110.1", {"start": v(61.48, -28.7) * mm, "mid": v(57.72, -34.46) * mm, "end": v(56.77, -41.28) * mm});
            skArc(sketch, "E110.2", {"start": v(72.34, -24.95) * mm, "mid": v(66.6, -25.91) * mm, "end": v(61.48, -28.7) * mm});
            skLineSegment(sketch, "E111.0", {"start": v(72.9, -24.96) * mm, "end": v(72.34, -24.95) * mm});
            skCircle(sketch, "E112", {"center": v(-150.5, 94.9) * mm, "radius": 1.63 * mm});
            skCircle(sketch, "E113", {"center": v(-126.5, 85.9) * mm, "radius": 1.63 * mm});
            skLineSegment(sketch, "E114.bottom", {"start": v(-145.4, 97.67) * mm, "end": v(-131.6, 97.67) * mm});
            skLineSegment(sketch, "E114.top", {"start": v(-145.4, 83.12) * mm, "end": v(-131.6, 83.12) * mm});
            skLineSegment(sketch, "E114.left", {"start": v(-146.78, 96.3) * mm, "end": v(-146.78, 84.5) * mm});
            skLineSegment(sketch, "E114.right", {"start": v(-130.23, 96.3) * mm, "end": v(-130.23, 84.5) * mm});
            skPoint(sketch, "E115.visualSharp", {"position": v(-146.78, 97.67) * mm});
            skArc(sketch, "E115.filletArc", {"start": v(-145.4, 97.67) * mm, "mid": v(-146.37, 97.27) * mm, "end": v(-146.78, 96.3) * mm});
            skPoint(sketch, "E116.visualSharp", {"position": v(-130.23, 97.67) * mm});
            skArc(sketch, "E116.filletArc", {"start": v(-130.23, 96.3) * mm, "mid": v(-130.63, 97.27) * mm, "end": v(-131.6, 97.67) * mm});
            skPoint(sketch, "E117.visualSharp", {"position": v(-130.23, 83.12) * mm});
            skArc(sketch, "E117.filletArc", {"start": v(-131.6, 83.12) * mm, "mid": v(-130.63, 83.53) * mm, "end": v(-130.23, 84.5) * mm});
            skPoint(sketch, "E118.visualSharp", {"position": v(-146.78, 83.12) * mm});
            skArc(sketch, "E118.filletArc", {"start": v(-146.78, 84.5) * mm, "mid": v(-146.37, 83.53) * mm, "end": v(-145.4, 83.12) * mm});
            skCircle(sketch, "E119", {"center": v(150.5, 90.4) * mm, "radius": 4.05 * mm});
            skCircle(sketch, "E120", {"center": v(116, 90.4) * mm, "radius": 1.6 * mm});
            skCircle(sketch, "E121", {"center": v(138, 90.4) * mm, "radius": 1.6 * mm});
            skLineSegment(sketch, "E122.bottom", {"start": v(121, 97.18) * mm, "end": v(133, 97.18) * mm});
            skLineSegment(sketch, "E122.top", {"start": v(121, 83.62) * mm, "end": v(133, 83.62) * mm});
            skLineSegment(sketch, "E122.left", {"start": v(119.73, 95.9) * mm, "end": v(119.73, 84.9) * mm});
            skLineSegment(sketch, "E122.right", {"start": v(134.28, 95.9) * mm, "end": v(134.28, 84.9) * mm});
            skPoint(sketch, "E123.visualSharp", {"position": v(119.73, 97.18) * mm});
            skArc(sketch, "E123.filletArc", {"start": v(121, 97.18) * mm, "mid": v(120.1, 96.8) * mm, "end": v(119.73, 95.9) * mm});
            skPoint(sketch, "E124.visualSharp", {"position": v(134.28, 97.18) * mm});
            skArc(sketch, "E124.filletArc", {"start": v(134.28, 95.9) * mm, "mid": v(133.9, 96.8) * mm, "end": v(133, 97.18) * mm});
            skPoint(sketch, "E125.visualSharp", {"position": v(134.28, 83.62) * mm});
            skArc(sketch, "E125.filletArc", {"start": v(133, 83.62) * mm, "mid": v(133.9, 84) * mm, "end": v(134.28, 84.9) * mm});
            skPoint(sketch, "E126.visualSharp", {"position": v(119.73, 83.62) * mm});
            skArc(sketch, "E126.filletArc", {"start": v(119.73, 84.9) * mm, "mid": v(120.1, 84) * mm, "end": v(121, 83.62) * mm});
            skCircle(sketch, "E127", {"center": v(0, -99.8) * mm, "radius": 6 * mm});
            skSolve(sketch);
        }
        {
            var Q0;
            Q0=qSketchRegion(id+"F0",true);
            extrude(context, id + "F1", {"entities" : qUnion([Q0]), "depth" : 3 * mm});
        }
    });
